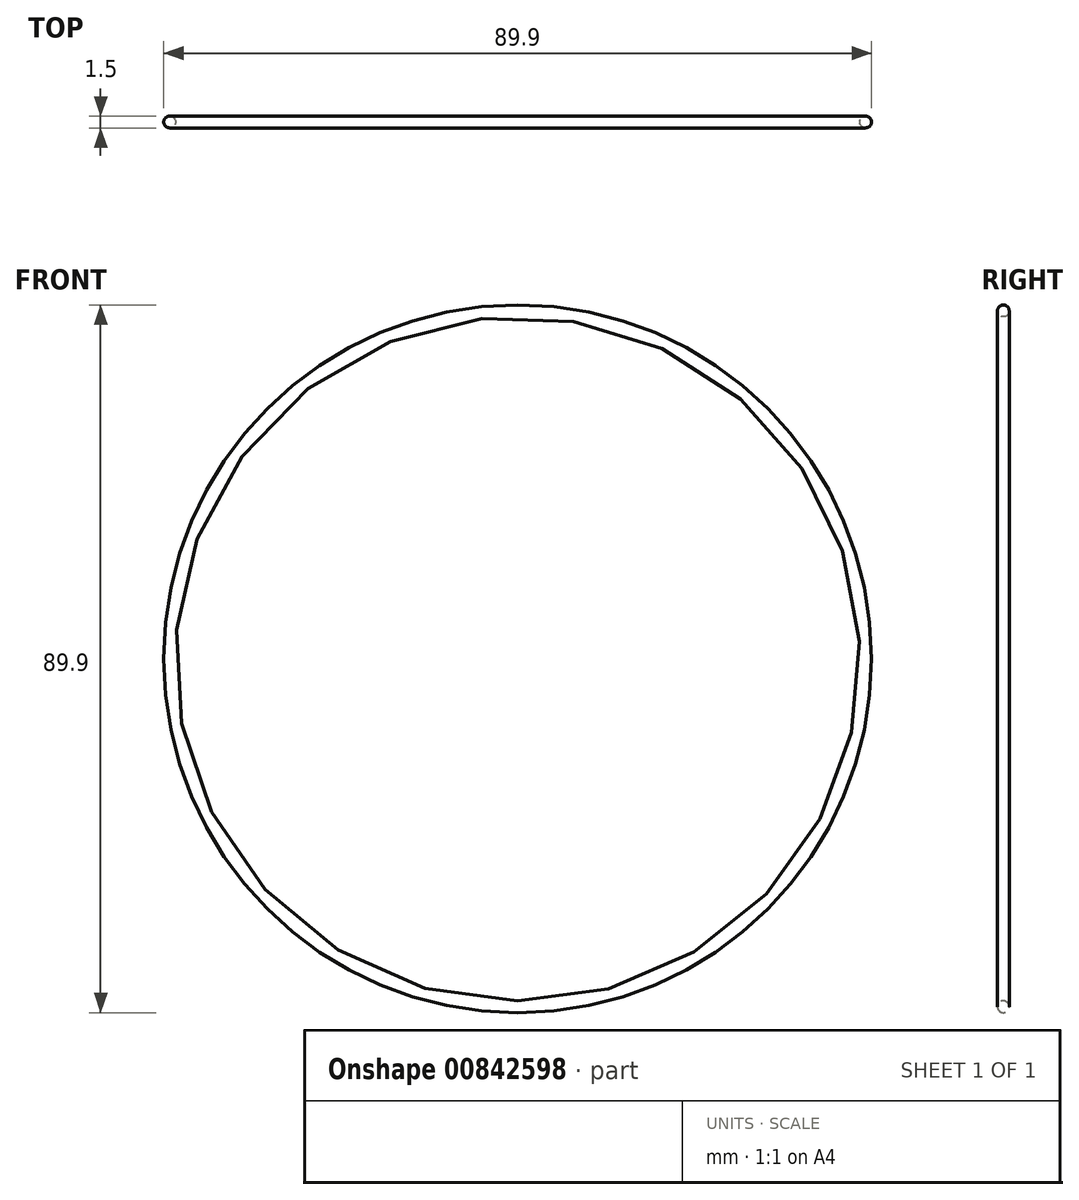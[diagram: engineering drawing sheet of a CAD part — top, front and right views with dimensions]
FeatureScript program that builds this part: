
annotation { "Feature Type Name" : "Feature", "Feature Type Description" : "" }
export const myFeature = defineFeature(function(context is Context, id is Id, definition is map)
    precondition{}
    {
        {
            var Q0;
            Q0=qCreatedBy(makeId("Right.planeOp"),FACE);
            var sketch = newSketch(context, id + "F0", { "sketchPlane" : qUnion([Q0])});
            skCircle(sketch, "E0", {"center": v(0, 44.2) * mm, "radius": 0.75 * mm});
            skLineSegment(sketch, "E1", {"start": v(-20.22, 0) * mm, "end": v(0, 0) * mm, "construction": true});
            skSolve(sketch);
        }
        {
            var Q0;
            Q0 = qSketchRegion(id + "F0", true);
            var Q1;
            Q1=sQuery(id+"F0.wireOp",EDGE,"E1");
            revolve(context, id + "F1", {"surfaceOperationType" : NewSurfaceOperationType.NEW, "entities" : qUnion([Q0]), "axis" : qUnion([Q1]), "revolveType" : RevolveType.FULL});
        }
    });
